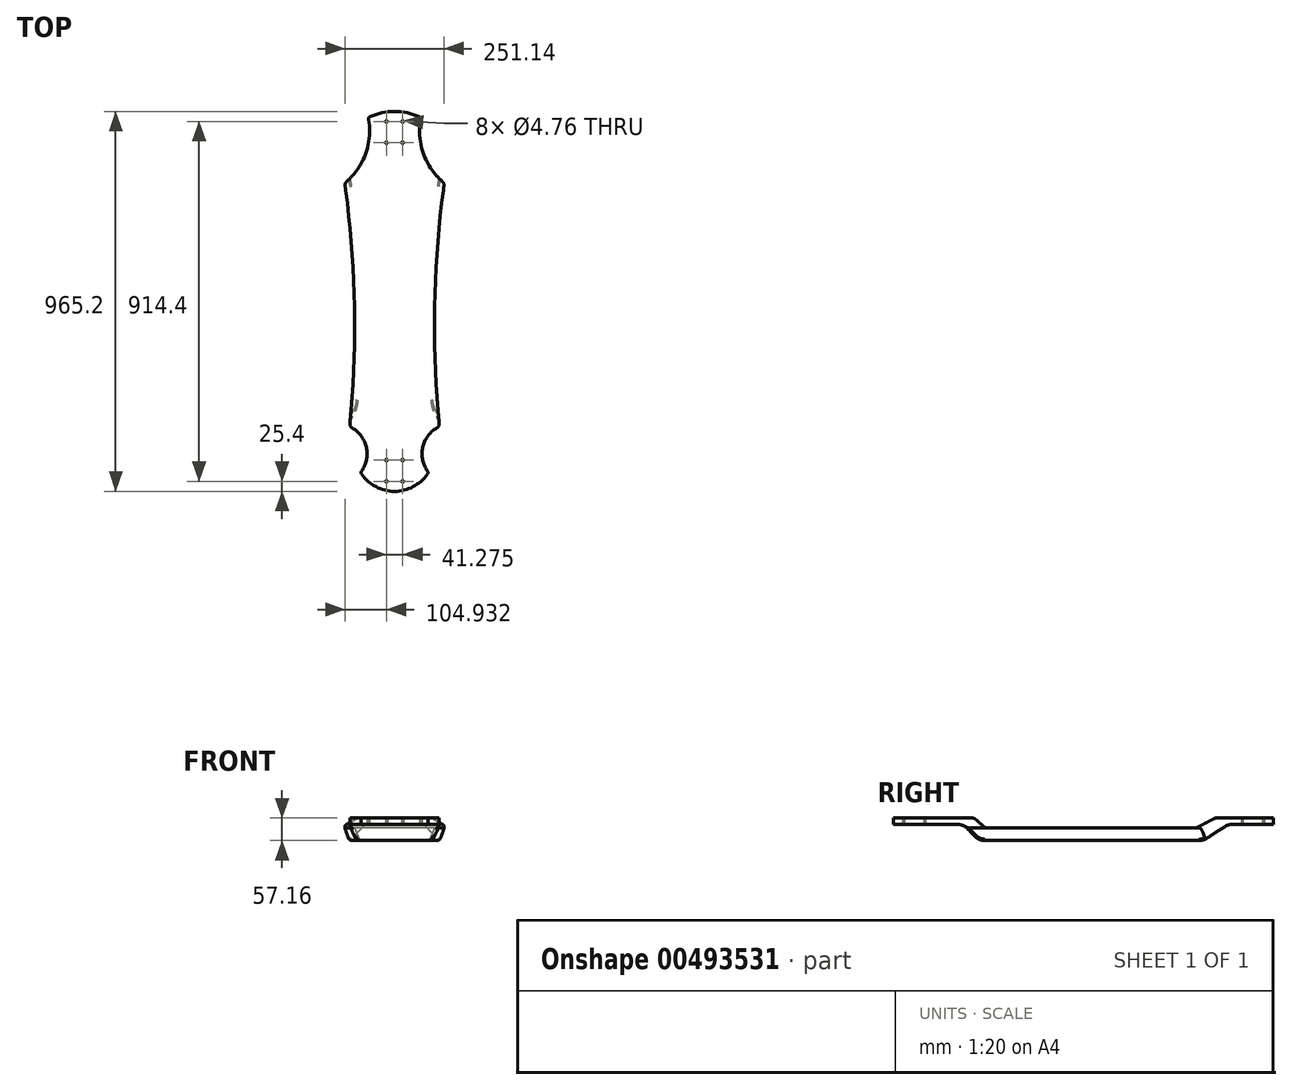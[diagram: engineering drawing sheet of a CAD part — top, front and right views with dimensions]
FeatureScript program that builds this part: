
annotation { "Feature Type Name" : "Feature", "Feature Type Description" : "" }
export const myFeature = defineFeature(function(context is Context, id is Id, definition is map)
    precondition{}
    {
        {
            var Q0;
            Q0=qCreatedBy(makeId("Front.planeOp"),FACE);
            var sketch = newSketch(context, id + "F0", { "sketchPlane" : qUnion([Q0])});
            skLineSegment(sketch, "E0", {"start": v(0, -7.64) * mm, "end": v(0, -34.1) * mm});
            skLineSegment(sketch, "E1", {"start": v(124.2, -17.61) * mm, "end": v(127.92, 6.58) * mm});
            skLineSegment(sketch, "E2", {"start": v(127.92, 6.58) * mm, "end": v(81, -6.71) * mm});
            skLineSegment(sketch, "E3", {"start": v(81, -6.71) * mm, "end": v(0, -7.64) * mm});
            skSolve(sketch);
        }
        {
            var Q0;
            Q0=qCreatedBy(makeId("Top.planeOp"),FACE);
            var sketch = newSketch(context, id + "F1", { "sketchPlane" : qUnion([Q0])});
            skLineSegment(sketch, "E4", {"start": v(0, 482.6) * mm, "end": v(0, -482.6) * mm});
            skArc(sketch, "E5", {"start": v(62.35, 469.26) * mm, "mid": v(31.88, 479.23) * mm, "end": v(0, 482.6) * mm});
            skArc(sketch, "E6", {"start": v(125.45, 293.59) * mm, "mid": v(102.12, -7.66) * mm, "end": v(113.48, -309.6) * mm});
            skArc(sketch, "E7", {"start": v(107.3, -321.74) * mm, "mid": v(71.55, -371.32) * mm, "end": v(83.74, -431.22) * mm});
            skArc(sketch, "E8", {"start": v(0, -482.6) * mm, "mid": v(47.35, -470.9) * mm, "end": v(83.79, -438.46) * mm});
            skLineSegment(sketch, "E9", {"start": v(0, 0) * mm, "end": v(127, 0) * mm, "construction": true});
            skLineSegment(sketch, "E10", {"start": v(127, 0) * mm, "end": v(127, 482.6) * mm, "construction": true});
            skLineSegment(sketch, "E11", {"start": v(127, 0) * mm, "end": v(127, -482.6) * mm, "construction": true});
            skLineSegment(sketch, "E12", {"start": v(127, -482.6) * mm, "end": v(0, -482.6) * mm, "construction": true});
            skLineSegment(sketch, "E13", {"start": v(0, 482.6) * mm, "end": v(127, 482.6) * mm, "construction": true});
            skLineSegment(sketch, "E14", {"start": v(114.3, -318.08) * mm, "end": v(2732.4, -318.08) * mm, "construction": true});
            skLineSegment(sketch, "E15", {"start": v(2732.4, 304.8) * mm, "end": v(127, 304.8) * mm, "construction": true});
            skLineSegment(sketch, "E16", {"start": v(2732.4, -318.08) * mm, "end": v(2732.4, 304.8) * mm, "construction": true});
            skPoint(sketch, "E17.visualSharp", {"position": v(127, 304.8) * mm});
            skArc(sketch, "E17.filletArc", {"start": v(125.45, 293.59) * mm, "mid": v(124.78, 299.71) * mm, "end": v(121.29, 304.8) * mm});
            skPoint(sketch, "E18.visualSharp", {"position": v(114.3, -318.08) * mm});
            skArc(sketch, "E18.filletArc", {"start": v(107.3, -321.74) * mm, "mid": v(112.15, -316.57) * mm, "end": v(113.48, -309.6) * mm});
            skPoint(sketch, "E19.visualSharp", {"position": v(86.3, -434.63) * mm});
            skArc(sketch, "E19.filletArc", {"start": v(83.79, -438.46) * mm, "mid": v(84.9, -434.83) * mm, "end": v(83.74, -431.22) * mm});
            skArc(sketch, "E20", {"start": v(66, 462.39) * mm, "mid": v(73.17, 376.4) * mm, "end": v(121.29, 304.8) * mm});
            skPoint(sketch, "E21.visualSharp", {"position": v(66.9, 467.13) * mm});
            skArc(sketch, "E21.filletArc", {"start": v(66, 462.39) * mm, "mid": v(65.36, 466.45) * mm, "end": v(62.35, 469.26) * mm});
            skSolve(sketch);
        }
        {
            var Q0;
            Q0 = qSketchRegion(id + "F1", true);
            extrude(context, id + "F2", {"entities" : qUnion([Q0]), "depth" : 57.15 * mm, "offsetDistance" : 25.4 * mm, "symmetric" : true});
        }
        {
            var Q0;
            Q0=qCreatedBy(makeId("Right.planeOp"),FACE);
            var sketch = newSketch(context, id + "F3", { "sketchPlane" : qUnion([Q0])});
            skLineSegment(sketch, "E22", {"start": v(482.6, 28.58) * mm, "end": v(338.43, 28.57) * mm});
            skLineSegment(sketch, "E23", {"start": v(330.97, 26.71) * mm, "end": v(290.24, 5.04) * mm});
            skLineSegment(sketch, "E24", {"start": v(282.78, 3.18) * mm, "end": v(-243.24, 3.17) * mm});
            skLineSegment(sketch, "E25", {"start": v(-253.92, 7.3) * mm, "end": v(-272.76, 24.44) * mm});
            skLineSegment(sketch, "E26", {"start": v(-283.44, 28.58) * mm, "end": v(-482.6, 28.57) * mm});
            skLineSegment(sketch, "E27", {"start": v(-482.6, 28.57) * mm, "end": v(-482.6, 12.7) * mm});
            skLineSegment(sketch, "E28", {"start": v(-482.6, 12.7) * mm, "end": v(-321.48, 12.7) * mm});
            skLineSegment(sketch, "E29", {"start": v(-293.49, 0.44) * mm, "end": v(-278.01, -16.32) * mm});
            skLineSegment(sketch, "E30", {"start": v(-250.02, -28.58) * mm, "end": v(293.5, -28.57) * mm});
            skLineSegment(sketch, "E31", {"start": v(314.27, -22.42) * mm, "end": v(358.83, 6.54) * mm});
            skLineSegment(sketch, "E32", {"start": v(379.6, 12.7) * mm, "end": v(482.6, 12.7) * mm});
            skLineSegment(sketch, "E33", {"start": v(482.6, 12.7) * mm, "end": v(482.6, 28.58) * mm});
            skPoint(sketch, "E34.visualSharp", {"position": v(334.46, 28.57) * mm});
            skArc(sketch, "E34.filletArc", {"start": v(338.43, 28.57) * mm, "mid": v(334.58, 28.1) * mm, "end": v(330.97, 26.71) * mm});
            skPoint(sketch, "E35.visualSharp", {"position": v(-277.3, 28.58) * mm});
            skArc(sketch, "E35.filletArc", {"start": v(-272.76, 24.44) * mm, "mid": v(-277.72, 27.5) * mm, "end": v(-283.44, 28.58) * mm});
            skPoint(sketch, "E36.visualSharp", {"position": v(286.74, 3.18) * mm});
            skArc(sketch, "E36.filletArc", {"start": v(282.78, 3.17) * mm, "mid": v(286.62, 3.65) * mm, "end": v(290.24, 5.04) * mm});
            skPoint(sketch, "E37.visualSharp", {"position": v(-249.38, 3.17) * mm});
            skArc(sketch, "E37.filletArc", {"start": v(-253.92, 7.3) * mm, "mid": v(-248.97, 4.24) * mm, "end": v(-243.24, 3.18) * mm});
            skPoint(sketch, "E38.visualSharp", {"position": v(368.3, 12.7) * mm});
            skArc(sketch, "E38.filletArc", {"start": v(379.6, 12.7) * mm, "mid": v(368.77, 11.13) * mm, "end": v(358.83, 6.54) * mm});
            skPoint(sketch, "E39.visualSharp", {"position": v(304.8, -28.57) * mm});
            skArc(sketch, "E39.filletArc", {"start": v(293.5, -28.57) * mm, "mid": v(304.33, -27) * mm, "end": v(314.27, -22.42) * mm});
            skPoint(sketch, "E40.visualSharp", {"position": v(-266.7, -28.58) * mm});
            skArc(sketch, "E40.filletArc", {"start": v(-278.01, -16.32) * mm, "mid": v(-265.3, -25.38) * mm, "end": v(-250.02, -28.58) * mm});
            skPoint(sketch, "E41.visualSharp", {"position": v(-304.8, 12.7) * mm});
            skArc(sketch, "E41.filletArc", {"start": v(-293.49, 0.44) * mm, "mid": v(-306.2, 9.5) * mm, "end": v(-321.48, 12.7) * mm});
            skLineSegment(sketch, "E42.bottom", {"start": v(482.6, 28.58) * mm, "end": v(-482.6, 28.57) * mm});
            skLineSegment(sketch, "E42.top", {"start": v(482.6, -28.57) * mm, "end": v(-482.6, -28.58) * mm});
            skLineSegment(sketch, "E42.left", {"start": v(482.6, 28.58) * mm, "end": v(482.6, -28.57) * mm});
            skLineSegment(sketch, "E42.right", {"start": v(-482.6, 28.57) * mm, "end": v(-482.6, -28.58) * mm});
            skSolve(sketch);
        }
        {
            var Q0;
            Q0=makeQuery(id+"F3.imprint","IMPRINT",FACE,{"disambiguationData":[TD([[makeQuery(id+"F3.imprint","IMPRINT",EDGE,{"derivedFrom":sQuery(id+"F3.wireOp",EDGE,"E23")}),-1.0]])]});
            var Q1;
            Q1=makeQuery(id+"F3.imprint","IMPRINT",FACE,{"disambiguationData":[TD([[makeQuery(id+"F3.imprint","IMPRINT",EDGE,{"derivedFrom":sQuery(id+"F3.wireOp",EDGE,"E31")}),-1.0]])]});
            var Q2;
            {var subQ0=sQuery(id+"F3.wireOp",EDGE,"E28");Q2=makeQuery(id+"F3.imprint","IMPRINT",FACE,{"disambiguationData":[TD([[makeQuery(id+"F3.imprint","IMPRINT",EDGE,{"derivedFrom":subQ0}),-1.0]])]});}
            extrude(context, id + "F4", {"entities" : qUnion([Q0, Q1, Q2]), "operationType" : NewBodyOperationType.REMOVE, "endBound" : BoundingType.THROUGH_ALL, "depth" : 25.4 * mm, "offsetDistance" : 25.4 * mm});
        }
        {
            var Q0;
            Q0=makeQuery(id+"F2.opExtrude","SWEPT_BODY",BODY,{"disambiguationData":[OSD([sQuery(id+"F1.wireOp",EDGE,"E4"),sQuery(id+"F1.wireOp",EDGE,"E5"),sQuery(id+"F1.wireOp",EDGE,"TCkLRzHp-wnxz-PYhF-fAcJ-VPnlEKGKHynH"),sQuery(id+"F1.wireOp",EDGE,"E6"),sQuery(id+"F1.wireOp",EDGE,"E7"),sQuery(id+"F1.wireOp",EDGE,"E8")])]});
            var Q1;
            Q1=qCreatedBy(makeId("Right.planeOp"),FACE);
            mirror(context, id + "F5", {"operationType" : NewBodyOperationType.ADD, "entities" : qUnion([Q0]), "mirrorPlane" : qUnion([Q1])});
        }
        {
            var Q0;
            Q0=qCreatedBy(makeId("Top.planeOp"),FACE);
            var sketch = newSketch(context, id + "F6", { "sketchPlane" : qUnion([Q0])});
            skLineSegment(sketch, "E43", {"start": v(0, -457.2) * mm, "end": v(0, 457.2) * mm, "construction": true});
            skLineSegment(sketch, "E44", {"start": v(-20.64, -457.2) * mm, "end": v(-20.64, -403.23) * mm, "construction": true});
            skLineSegment(sketch, "E45", {"start": v(-20.64, -403.23) * mm, "end": v(20.64, -403.23) * mm, "construction": true});
            skLineSegment(sketch, "E46", {"start": v(20.64, -403.23) * mm, "end": v(20.64, -457.2) * mm, "construction": true});
            skLineSegment(sketch, "E47", {"start": v(20.64, -457.2) * mm, "end": v(-20.64, -457.2) * mm, "construction": true});
            skLineSegment(sketch, "E48", {"start": v(0, 457.2) * mm, "end": v(-20.64, 457.2) * mm, "construction": true});
            skLineSegment(sketch, "E49", {"start": v(-20.64, 457.2) * mm, "end": v(-20.64, 403.23) * mm, "construction": true});
            skLineSegment(sketch, "E50", {"start": v(-20.64, 403.23) * mm, "end": v(20.64, 403.23) * mm, "construction": true});
            skLineSegment(sketch, "E51", {"start": v(20.64, 403.23) * mm, "end": v(20.64, 457.2) * mm, "construction": true});
            skLineSegment(sketch, "E52", {"start": v(20.64, 457.2) * mm, "end": v(0, 457.2) * mm, "construction": true});
            skCircle(sketch, "E53", {"center": v(-20.64, 403.23) * mm, "radius": 2.38 * mm});
            skCircle(sketch, "E54", {"center": v(20.64, 403.23) * mm, "radius": 2.38 * mm});
            skCircle(sketch, "E55", {"center": v(20.64, 457.2) * mm, "radius": 2.38 * mm});
            skCircle(sketch, "E56", {"center": v(-20.64, 457.2) * mm, "radius": 2.38 * mm});
            skCircle(sketch, "E57", {"center": v(-20.64, -457.2) * mm, "radius": 2.38 * mm});
            skCircle(sketch, "E58", {"center": v(20.64, -457.2) * mm, "radius": 2.38 * mm});
            skCircle(sketch, "E59", {"center": v(20.64, -403.23) * mm, "radius": 2.38 * mm});
            skCircle(sketch, "E60", {"center": v(-20.64, -403.23) * mm, "radius": 2.38 * mm});
            skSolve(sketch);
        }
        {
            var Q0;
            Q0 = qSketchRegion(id + "F6", true);
            extrude(context, id + "F7", {"entities" : qUnion([Q0]), "operationType" : NewBodyOperationType.REMOVE, "endBound" : BoundingType.THROUGH_ALL, "depth" : 25.4 * mm, "offsetDistance" : 25.4 * mm});
        }
        {
            var Q0;
            Q0=makeQuery(id+"F2.opExtrude","CAP_EDGE",EDGE,{"disambiguationData":[OSD([sQuery(id+"F1.wireOp",EDGE,"E6")])],"isStart":true});
            var Q1;
            Q1=makeQuery(id+"F5.opPattern","COPY",EDGE,{"derivedFrom":makeQuery(id+"F2.opExtrude","CAP_EDGE",EDGE,{"disambiguationData":[OSD([sQuery(id+"F1.wireOp",EDGE,"E6")])],"isStart":true}),"instanceName":"1"});
            chamfer(context, id + "F8", {"entities" : qUnion([Q0, Q1]), "chamferType" : ChamferType.TWO_OFFSETS, "width1" : 12.7 * mm, "oppositeDirection" : false, "width2" : 31.75 * mm});
        }
        {
            var Q0;
            {var subQ0=sQuery(id+"F1.wireOp",EDGE,"E6");var subQ1=makeQuery(id+"F2.opExtrude","CAP_FACE",FACE,{"disambiguationData":[OSD([sQuery(id+"F1.wireOp",EDGE,"E4"),sQuery(id+"F1.wireOp",EDGE,"E5"),subQ0,sQuery(id+"F1.wireOp",EDGE,"E7"),sQuery(id+"F1.wireOp",EDGE,"E8"),sQuery(id+"F1.wireOp",EDGE,"E17.filletArc"),sQuery(id+"F1.wireOp",EDGE,"E18.filletArc"),sQuery(id+"F1.wireOp",EDGE,"E19.filletArc"),sQuery(id+"F1.wireOp",EDGE,"E20"),sQuery(id+"F1.wireOp",EDGE,"E21.filletArc")])],"isStart":true});Q0=makeQuery(id+"F8.opChamfer","BLEND_EDGE",EDGE,{"blendedFrom":[makeQuery(id+"F5.opPattern","COPY",EDGE,{"derivedFrom":makeQuery(id+"F2.opExtrude","CAP_EDGE",EDGE,{"disambiguationData":[OSD([subQ0])],"isStart":true}),"instanceName":"1"}),makeQuery(id+"F5.boolean.opBoolean","MERGE",FACE,{"derivedFrom":[subQ1,makeQuery(id+"F5.opPattern","COPY",FACE,{"derivedFrom":subQ1,"instanceName":"1"})]})],"blendedInto":[makeQuery(id+"F5.boolean.opBoolean","MERGE",FACE,{"derivedFrom":[subQ1,makeQuery(id+"F5.opPattern","COPY",FACE,{"derivedFrom":subQ1,"instanceName":"1"})]})]});}
            var Q1;
            {var subQ0=sQuery(id+"F1.wireOp",EDGE,"E6");var subQ1=makeQuery(id+"F2.opExtrude","CAP_FACE",FACE,{"disambiguationData":[OSD([sQuery(id+"F1.wireOp",EDGE,"E4"),sQuery(id+"F1.wireOp",EDGE,"E5"),subQ0,sQuery(id+"F1.wireOp",EDGE,"E7"),sQuery(id+"F1.wireOp",EDGE,"E8"),sQuery(id+"F1.wireOp",EDGE,"E17.filletArc"),sQuery(id+"F1.wireOp",EDGE,"E18.filletArc"),sQuery(id+"F1.wireOp",EDGE,"E19.filletArc"),sQuery(id+"F1.wireOp",EDGE,"E20"),sQuery(id+"F1.wireOp",EDGE,"E21.filletArc")])],"isStart":true});Q1=makeQuery(id+"F8.opChamfer","BLEND_EDGE",EDGE,{"blendedFrom":[makeQuery(id+"F2.opExtrude","CAP_EDGE",EDGE,{"disambiguationData":[OSD([subQ0])],"isStart":true}),makeQuery(id+"F5.boolean.opBoolean","MERGE",FACE,{"derivedFrom":[subQ1,makeQuery(id+"F5.opPattern","COPY",FACE,{"derivedFrom":subQ1,"instanceName":"1"})]})],"blendedInto":[makeQuery(id+"F5.boolean.opBoolean","MERGE",FACE,{"derivedFrom":[subQ1,makeQuery(id+"F5.opPattern","COPY",FACE,{"derivedFrom":subQ1,"instanceName":"1"})]})]});}
            fillet(context, id + "F9", {"entities" : qUnion([Q0, Q1]), "tangentPropagation" : true, "radius" : 5.08 * mm, "defaultsChanged" : false, "vertexSettings" : [], "allowEdgeOverflow" : false});
        }
    });
